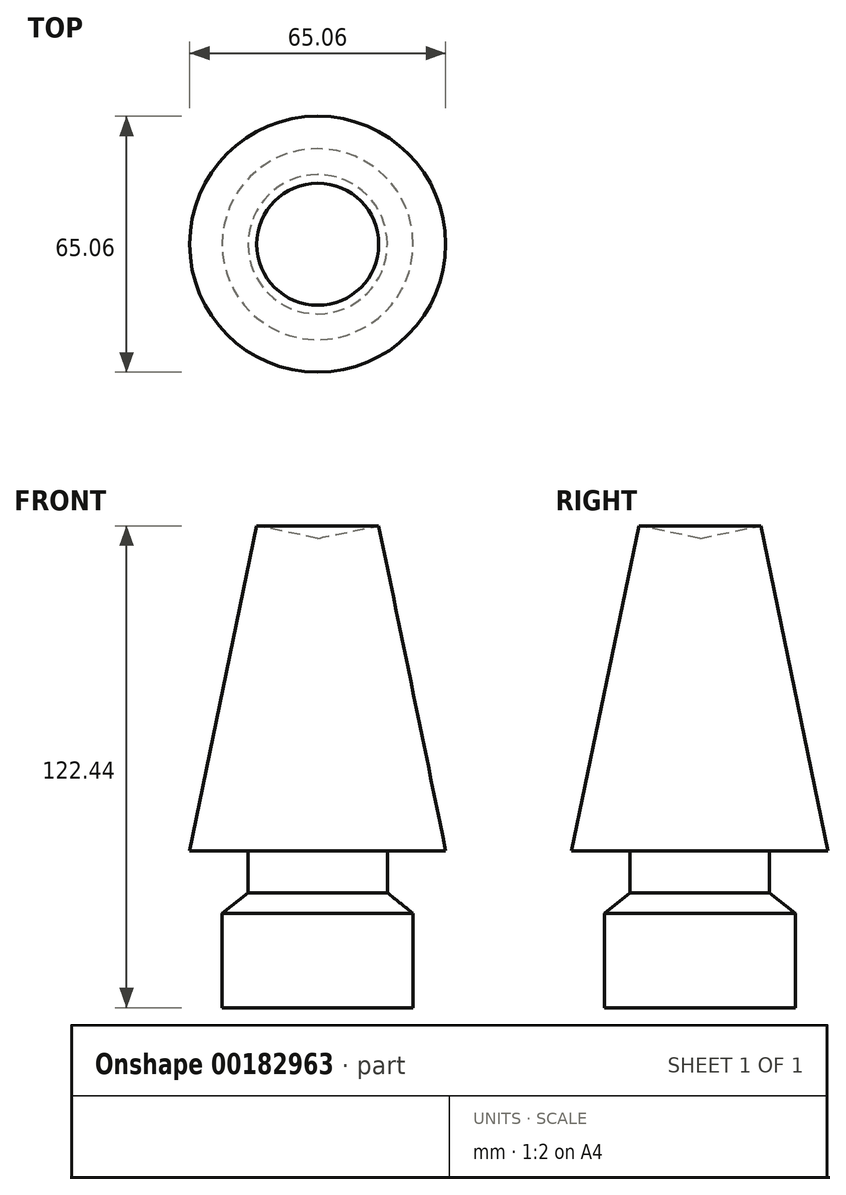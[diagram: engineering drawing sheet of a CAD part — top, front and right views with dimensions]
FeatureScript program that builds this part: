
annotation { "Feature Type Name" : "Feature", "Feature Type Description" : "" }
export const myFeature = defineFeature(function(context is Context, id is Id, definition is map)
    precondition{}
    {
        {
            var Q0;
            Q0=qCreatedBy(makeId("Front.planeOp"),FACE);
            var sketch = newSketch(context, id + "F0", { "sketchPlane" : qUnion([Q0])});
            skLineSegment(sketch, "E0", {"start": v(0, 0) * mm, "end": v(24.26, 0) * mm});
            skLineSegment(sketch, "E1", {"start": v(24.26, 0) * mm, "end": v(24.26, 23.91) * mm});
            skLineSegment(sketch, "E2", {"start": v(24.26, 23.91) * mm, "end": v(17.7, 29.2) * mm});
            skLineSegment(sketch, "E3", {"start": v(17.7, 29.2) * mm, "end": v(17.7, 39.83) * mm});
            skLineSegment(sketch, "E4", {"start": v(17.7, 39.83) * mm, "end": v(32.53, 39.83) * mm});
            skLineSegment(sketch, "E5", {"start": v(32.53, 39.83) * mm, "end": v(15.5, 122.44) * mm});
            skLineSegment(sketch, "E6", {"start": v(15.5, 122.44) * mm, "end": v(0, 119.24) * mm});
            skLineSegment(sketch, "E7", {"start": v(0, 119.24) * mm, "end": v(0, 0) * mm});
            skSolve(sketch);
        }
        {
            var Q0;
            Q0 = qSketchRegion(id + "F0", true);
            var Q1;
            Q1=sQuery(id+"F0.wireOp",EDGE,"E7");
            revolve(context, id + "F1", {"entities" : qUnion([Q0]), "axis" : qUnion([Q1]), "revolveType" : RevolveType.FULL});
        }
    });
